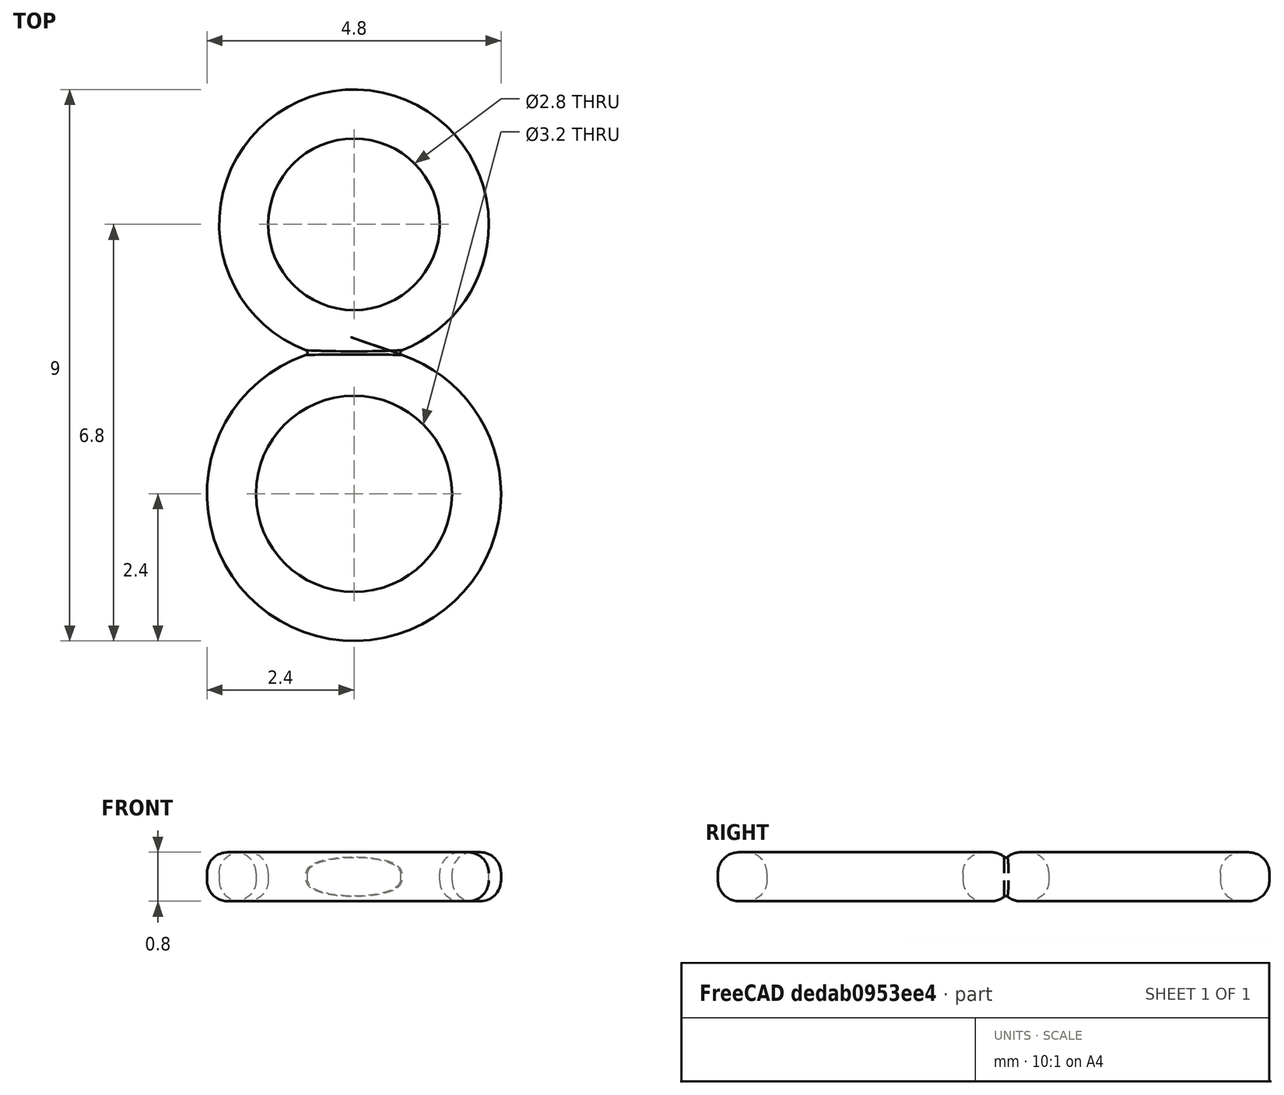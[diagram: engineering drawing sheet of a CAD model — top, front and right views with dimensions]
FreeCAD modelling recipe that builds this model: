
FCSTD DOCUMENT  (FreeCAD 0.16R6712 (Git))
Label: 8
License: All rights reserved
LicenseURL: http://en.wikipedia.org/wiki/All_rights_reserved
objects: PartDesign::Fillet×3, Sketcher::SketchObject×2, PartDesign::Pad×2, Part::MultiFuse×1, Mesh::Feature×1
note: 10 computed .brp shape members not serialized (recipe doc carries the construction recipe); baked Part::Feature solids carry a one-line shape summary decoded from their .brp

FEATURE [Sketcher::SketchObject] Sketch
  sketch-geometry (2):
    g0: Circle CenterX=0 CenterY=2.4 CenterZ=0 NormalX=0 NormalY=0 NormalZ=1 Radius=1.6
    g1: Circle CenterX=0 CenterY=2.4 CenterZ=0 NormalX=0 NormalY=0 NormalZ=1 Radius=2.4
  constraints (5):
    c: Coincident(g1,g0)
    c: Radius(g1) = 2.4
    c: Radius(g0) = 1.6
    c: Tangent(g1,g-1)
    c: PointOnObject(g0,g-2)
FEATURE [PartDesign::Pad] Pad
  Length = 0.8
  Length2 = 100
  Midplane = true
  Sketch = -> Sketch
  Type = 0
FEATURE [Sketcher::SketchObject] Sketch001
  sketch-geometry (2):
    g0: Circle CenterX=0 CenterY=6.8 CenterZ=0 NormalX=0 NormalY=0 NormalZ=1 Radius=2.2
    g1: Circle CenterX=0 CenterY=6.8 CenterZ=0 NormalX=0 NormalY=0 NormalZ=1 Radius=1.4
  constraints (5):
    c: Coincident(g1,g0)
    c: PointOnObject(g0,g-2)
    c: Radius(g0) = 2.2
    c: Radius(g1) = 1.4
    c: DistanceY(g-1,g0) = 6.8
FEATURE [PartDesign::Pad] Pad001
  Length = 0.8
  Length2 = 100
  Midplane = true
  Sketch = -> Sketch001
  Type = 0
FEATURE [PartDesign::Fillet] Fillet
  Base = -> Pad001 [Edge2,Edge5,Edge3,Edge6]
  Radius = 0.34
FEATURE [PartDesign::Fillet] Fillet001
  Base = -> Pad [Edge2,Edge5,Edge3,Edge6]
  Radius = 0.34
FEATURE [Part::MultiFuse] Fusion
  Shapes = -> [Fillet,Fillet001]
FEATURE [PartDesign::Fillet] Fillet002
  Base = -> Fusion [Edge20,Edge16,Edge4,Edge11]
  Radius = 0.04
FEATURE [Mesh::Feature] Mesh  label="Fillet002 (Meshed)"
